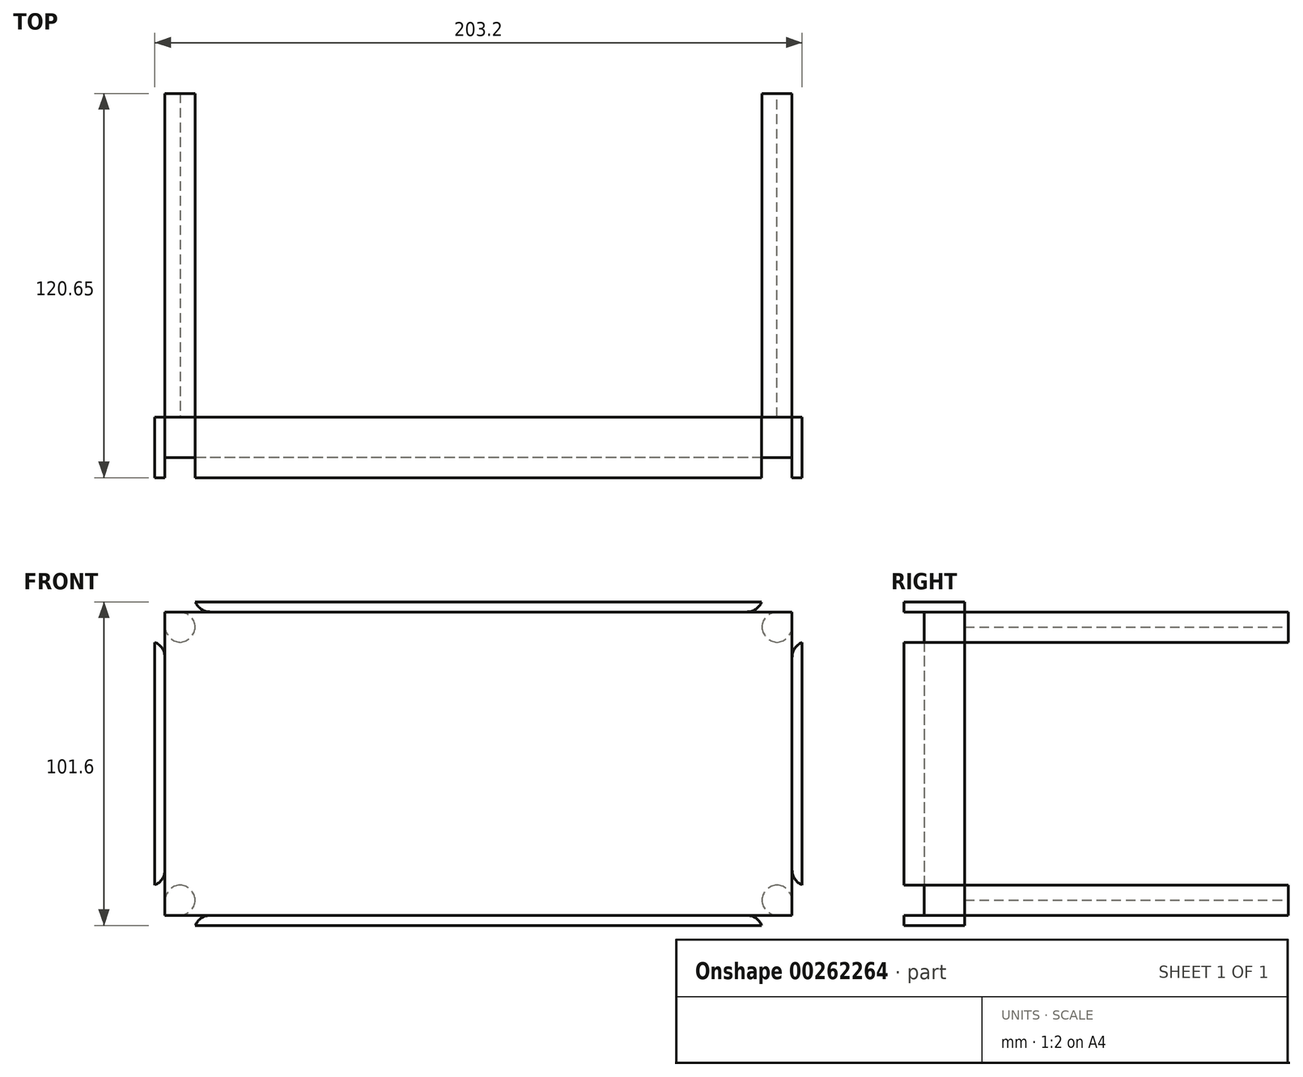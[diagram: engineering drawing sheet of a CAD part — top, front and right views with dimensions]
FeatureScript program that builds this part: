
annotation { "Feature Type Name" : "Feature", "Feature Type Description" : "" }
export const myFeature = defineFeature(function(context is Context, id is Id, definition is map)
    precondition{}
    {
        {
            var Q0;
            Q0=qCreatedBy(makeId("Front.planeOp"),FACE);
            var sketch = newSketch(context, id + "F0", { "sketchPlane" : qUnion([Q0])});
            skLineSegment(sketch, "E0.bottom", {"start": v(101.6, 50.8) * mm, "end": v(-101.6, 50.8) * mm});
            skLineSegment(sketch, "E0.top", {"start": v(101.6, -50.8) * mm, "end": v(-101.6, -50.8) * mm});
            skLineSegment(sketch, "E0.left", {"start": v(101.6, 50.8) * mm, "end": v(101.6, -50.8) * mm});
            skLineSegment(sketch, "E0.right", {"start": v(-101.6, 50.8) * mm, "end": v(-101.6, -50.8) * mm});
            skPoint(sketch, "E0.middle", {"position": v(0, 0) * mm});
            skLineSegment(sketch, "E1.bottom", {"start": v(98.43, 47.62) * mm, "end": v(-98.43, 47.62) * mm});
            skLineSegment(sketch, "E1.top", {"start": v(98.43, -47.63) * mm, "end": v(-98.43, -47.63) * mm});
            skLineSegment(sketch, "E1.left", {"start": v(98.43, 47.62) * mm, "end": v(98.43, -47.63) * mm});
            skLineSegment(sketch, "E1.right", {"start": v(-98.43, 47.63) * mm, "end": v(-98.43, -47.63) * mm});
            skLineSegment(sketch, "E2.bottom", {"start": v(-101.6, 50.8) * mm, "end": v(-88.9, 50.8) * mm});
            skLineSegment(sketch, "E2.top", {"start": v(-101.6, 38.1) * mm, "end": v(-88.9, 38.1) * mm});
            skLineSegment(sketch, "E2.left", {"start": v(-101.6, 50.8) * mm, "end": v(-101.6, 38.1) * mm});
            skLineSegment(sketch, "E2.right", {"start": v(-88.9, 50.8) * mm, "end": v(-88.9, 38.1) * mm});
            skLineSegment(sketch, "E3.bottom", {"start": v(-101.6, -50.8) * mm, "end": v(-88.9, -50.8) * mm});
            skLineSegment(sketch, "E3.top", {"start": v(-101.6, -38.1) * mm, "end": v(-88.9, -38.1) * mm});
            skLineSegment(sketch, "E3.left", {"start": v(-101.6, -50.8) * mm, "end": v(-101.6, -38.1) * mm});
            skLineSegment(sketch, "E3.right", {"start": v(-88.9, -50.8) * mm, "end": v(-88.9, -38.1) * mm});
            skLineSegment(sketch, "E4.bottom", {"start": v(101.6, -50.8) * mm, "end": v(88.9, -50.8) * mm});
            skLineSegment(sketch, "E4.top", {"start": v(101.6, -38.1) * mm, "end": v(88.9, -38.1) * mm});
            skLineSegment(sketch, "E4.left", {"start": v(101.6, -50.8) * mm, "end": v(101.6, -38.1) * mm});
            skLineSegment(sketch, "E4.right", {"start": v(88.9, -50.8) * mm, "end": v(88.9, -38.1) * mm});
            skLineSegment(sketch, "E5.bottom", {"start": v(101.6, 50.8) * mm, "end": v(88.9, 50.8) * mm});
            skLineSegment(sketch, "E5.top", {"start": v(101.6, 38.1) * mm, "end": v(88.9, 38.1) * mm});
            skLineSegment(sketch, "E5.left", {"start": v(101.6, 50.8) * mm, "end": v(101.6, 38.1) * mm});
            skLineSegment(sketch, "E5.right", {"start": v(88.9, 50.8) * mm, "end": v(88.9, 38.1) * mm});
            skSolve(sketch);
        }
        {
            var Q0;
            {var subQ19=sQuery(id+"F0.wireOp",EDGE,"E5.right");var subQ20=sQuery(id+"F0.wireOp",EDGE,"E1.bottom");var subQ21=makeQuery(id+"F0.imprint","INTERSECT",VERTEX,{"derivedFrom":[subQ20,subQ19]});Q0=makeQuery(id+"F0.imprint","IMPRINT",FACE,{"disambiguationData":[TD([[makeQuery(id+"F0.imprint","IMPRINT",EDGE,{"disambiguationData":[TD([[subQ21,-1.0]])],"derivedFrom":subQ20}),1.0]])]});}
            var Q1;
            {var subQ0=sQuery(id+"F0.wireOp",EDGE,"E1.right");var subQ1=sQuery(id+"F0.wireOp",EDGE,"E1.bottom");var subQ2=makeQuery(id+"F0.imprint","INTERSECT",VERTEX,{"derivedFrom":[subQ1,subQ0]});Q1=makeQuery(id+"F0.imprint","IMPRINT",FACE,{"disambiguationData":[TD([[makeQuery(id+"F0.imprint","IMPRINT",EDGE,{"disambiguationData":[TD([[subQ2,1.0]])],"derivedFrom":subQ1}),1.0]])]});}
            var Q2;
            {var subQ0=sQuery(id+"F0.wireOp",EDGE,"E1.right");var subQ1=sQuery(id+"F0.wireOp",EDGE,"E1.top");var subQ2=makeQuery(id+"F0.imprint","INTERSECT",VERTEX,{"derivedFrom":[subQ1,subQ0]});Q2=makeQuery(id+"F0.imprint","IMPRINT",FACE,{"disambiguationData":[TD([[makeQuery(id+"F0.imprint","IMPRINT",EDGE,{"disambiguationData":[TD([[subQ2,1.0]])],"derivedFrom":subQ1}),-1.0]])]});}
            var Q3;
            {var subQ0=sQuery(id+"F0.wireOp",EDGE,"E1.left");var subQ1=sQuery(id+"F0.wireOp",EDGE,"E1.bottom");var subQ2=makeQuery(id+"F0.imprint","INTERSECT",VERTEX,{"derivedFrom":[subQ1,subQ0]});Q3=makeQuery(id+"F0.imprint","IMPRINT",FACE,{"disambiguationData":[TD([[makeQuery(id+"F0.imprint","IMPRINT",EDGE,{"disambiguationData":[TD([[subQ2,-1.0]])],"derivedFrom":subQ1}),1.0]])]});}
            var Q4;
            {var subQ0=sQuery(id+"F0.wireOp",EDGE,"E1.left");var subQ1=sQuery(id+"F0.wireOp",EDGE,"E1.top");var subQ2=makeQuery(id+"F0.imprint","INTERSECT",VERTEX,{"derivedFrom":[subQ1,subQ0]});Q4=makeQuery(id+"F0.imprint","IMPRINT",FACE,{"disambiguationData":[TD([[makeQuery(id+"F0.imprint","IMPRINT",EDGE,{"disambiguationData":[TD([[subQ2,-1.0]])],"derivedFrom":subQ1}),-1.0]])]});}
            extrude(context, id + "F1", {"entities" : qUnion([Q0, Q1, Q2, Q3, Q4]), "depth" : 12.7 * mm});
        }
        {
            var Q0;
            {var subQ0=sQuery(id+"F0.wireOp",EDGE,"E0.right");Q0=makeQuery(id+"F0.imprint","IMPRINT",FACE,{"disambiguationData":[TD([[makeQuery(id+"F0.imprint","IMPRINT",EDGE,{"derivedFrom":subQ0}),1.0]])]});}
            var Q1;
            {var subQ8=sQuery(id+"F0.wireOp",EDGE,"E2.bottom");Q1=makeQuery(id+"F0.imprint","IMPRINT",FACE,{"disambiguationData":[TD([[makeQuery(id+"F0.imprint","IMPRINT",EDGE,{"derivedFrom":subQ8}),-1.0]])]});}
            var Q2;
            {var subQ0=sQuery(id+"F0.wireOp",EDGE,"E0.bottom");Q2=makeQuery(id+"F0.imprint","IMPRINT",FACE,{"disambiguationData":[TD([[makeQuery(id+"F0.imprint","IMPRINT",EDGE,{"derivedFrom":subQ0}),1.0]])]});}
            var Q3;
            {var subQ8=sQuery(id+"F0.wireOp",EDGE,"E5.bottom");Q3=makeQuery(id+"F0.imprint","IMPRINT",FACE,{"disambiguationData":[TD([[makeQuery(id+"F0.imprint","IMPRINT",EDGE,{"derivedFrom":subQ8}),1.0]])]});}
            var Q4;
            {var subQ0=sQuery(id+"F0.wireOp",EDGE,"E0.left");Q4=makeQuery(id+"F0.imprint","IMPRINT",FACE,{"disambiguationData":[TD([[makeQuery(id+"F0.imprint","IMPRINT",EDGE,{"derivedFrom":subQ0}),-1.0]])]});}
            var Q5;
            {var subQ0=sQuery(id+"F0.wireOp",EDGE,"E0.top");Q5=makeQuery(id+"F0.imprint","IMPRINT",FACE,{"disambiguationData":[TD([[makeQuery(id+"F0.imprint","IMPRINT",EDGE,{"derivedFrom":subQ0}),-1.0]])]});}
            var Q6;
            {var subQ4=sQuery(id+"F0.wireOp",EDGE,"E4.bottom");Q6=makeQuery(id+"F0.imprint","IMPRINT",FACE,{"disambiguationData":[TD([[makeQuery(id+"F0.imprint","IMPRINT",EDGE,{"derivedFrom":subQ4}),-1.0]])]});}
            var Q7;
            {var subQ4=sQuery(id+"F0.wireOp",EDGE,"E3.bottom");Q7=makeQuery(id+"F0.imprint","IMPRINT",FACE,{"disambiguationData":[TD([[makeQuery(id+"F0.imprint","IMPRINT",EDGE,{"derivedFrom":subQ4}),1.0]])]});}
            extrude(context, id + "F2", {"entities" : qUnion([Q0, Q1, Q2, Q3, Q4, Q5, Q6, Q7]), "depth" : 19.05 * mm});
        }
        {
            var Q0;
            {var subQ0=sQuery(id+"F0.wireOp",EDGE,"E1.right");var subQ1=sQuery(id+"F0.wireOp",EDGE,"E1.bottom");var subQ2=makeQuery(id+"F0.imprint","INTERSECT",VERTEX,{"derivedFrom":[subQ1,subQ0]});Q0=makeQuery(id+"F0.imprint","IMPRINT",FACE,{"disambiguationData":[TD([[makeQuery(id+"F0.imprint","IMPRINT",EDGE,{"disambiguationData":[TD([[subQ2,1.0]])],"derivedFrom":subQ1}),1.0]])]});}
            var Q1;
            {var subQ8=sQuery(id+"F0.wireOp",EDGE,"E2.bottom");Q1=makeQuery(id+"F0.imprint","IMPRINT",FACE,{"disambiguationData":[TD([[makeQuery(id+"F0.imprint","IMPRINT",EDGE,{"derivedFrom":subQ8}),-1.0]])]});}
            var Q2;
            {var subQ0=sQuery(id+"F0.wireOp",EDGE,"E1.right");var subQ1=sQuery(id+"F0.wireOp",EDGE,"E1.top");var subQ2=makeQuery(id+"F0.imprint","INTERSECT",VERTEX,{"derivedFrom":[subQ1,subQ0]});Q2=makeQuery(id+"F0.imprint","IMPRINT",FACE,{"disambiguationData":[TD([[makeQuery(id+"F0.imprint","IMPRINT",EDGE,{"disambiguationData":[TD([[subQ2,1.0]])],"derivedFrom":subQ1}),-1.0]])]});}
            var Q3;
            {var subQ4=sQuery(id+"F0.wireOp",EDGE,"E3.bottom");Q3=makeQuery(id+"F0.imprint","IMPRINT",FACE,{"disambiguationData":[TD([[makeQuery(id+"F0.imprint","IMPRINT",EDGE,{"derivedFrom":subQ4}),1.0]])]});}
            var Q4;
            {var subQ0=sQuery(id+"F0.wireOp",EDGE,"E1.left");var subQ1=sQuery(id+"F0.wireOp",EDGE,"E1.top");var subQ2=makeQuery(id+"F0.imprint","INTERSECT",VERTEX,{"derivedFrom":[subQ1,subQ0]});Q4=makeQuery(id+"F0.imprint","IMPRINT",FACE,{"disambiguationData":[TD([[makeQuery(id+"F0.imprint","IMPRINT",EDGE,{"disambiguationData":[TD([[subQ2,-1.0]])],"derivedFrom":subQ1}),-1.0]])]});}
            var Q5;
            {var subQ4=sQuery(id+"F0.wireOp",EDGE,"E4.bottom");Q5=makeQuery(id+"F0.imprint","IMPRINT",FACE,{"disambiguationData":[TD([[makeQuery(id+"F0.imprint","IMPRINT",EDGE,{"derivedFrom":subQ4}),-1.0]])]});}
            var Q6;
            {var subQ0=sQuery(id+"F0.wireOp",EDGE,"E1.left");var subQ1=sQuery(id+"F0.wireOp",EDGE,"E1.bottom");var subQ2=makeQuery(id+"F0.imprint","INTERSECT",VERTEX,{"derivedFrom":[subQ1,subQ0]});Q6=makeQuery(id+"F0.imprint","IMPRINT",FACE,{"disambiguationData":[TD([[makeQuery(id+"F0.imprint","IMPRINT",EDGE,{"disambiguationData":[TD([[subQ2,-1.0]])],"derivedFrom":subQ1}),1.0]])]});}
            var Q7;
            {var subQ8=sQuery(id+"F0.wireOp",EDGE,"E5.bottom");Q7=makeQuery(id+"F0.imprint","IMPRINT",FACE,{"disambiguationData":[TD([[makeQuery(id+"F0.imprint","IMPRINT",EDGE,{"derivedFrom":subQ8}),1.0]])]});}
            extrude(context, id + "F3", {"entities" : qUnion([Q0, Q1, Q2, Q3, Q4, Q5, Q6, Q7]), "oppositeDirection" : true, "depth" : 101.6 * mm});
        }
        {
            var Q0;
            Q0=makeQuery(id+"F2.opExtrude","SWEPT_EDGE",EDGE,{"disambiguationData":[OSD([sQuery(id+"F0.wireOp",EDGE,"E1.top"),sQuery(id+"F0.wireOp",EDGE,"E1.left")])]});
            var Q1;
            Q1=makeQuery(id+"F2.opExtrude","SWEPT_EDGE",EDGE,{"disambiguationData":[OSD([sQuery(id+"F0.wireOp",EDGE,"E1.bottom"),sQuery(id+"F0.wireOp",EDGE,"E1.left")])]});
            var Q2;
            Q2=makeQuery(id+"F2.opExtrude","SWEPT_EDGE",EDGE,{"disambiguationData":[OSD([sQuery(id+"F0.wireOp",EDGE,"E1.top"),sQuery(id+"F0.wireOp",EDGE,"E1.right")])]});
            var Q3;
            Q3=makeQuery(id+"F2.opExtrude","SWEPT_EDGE",EDGE,{"disambiguationData":[OSD([sQuery(id+"F0.wireOp",EDGE,"E1.bottom"),sQuery(id+"F0.wireOp",EDGE,"E1.right")])]});
            var Q4;
            Q4=makeQuery(id+"F2.opExtrude","SWEPT_EDGE",EDGE,{"disambiguationData":[OSD([sQuery(id+"F0.wireOp",EDGE,"E4.bottom"),sQuery(id+"F0.wireOp",EDGE,"E4.left")])]});
            var Q5;
            Q5=makeQuery(id+"F2.opExtrude","SWEPT_EDGE",EDGE,{"disambiguationData":[OSD([sQuery(id+"F0.wireOp",EDGE,"E5.bottom"),sQuery(id+"F0.wireOp",EDGE,"E5.left")])]});
            var Q6;
            Q6=makeQuery(id+"F2.opExtrude","SWEPT_EDGE",EDGE,{"disambiguationData":[OSD([sQuery(id+"F0.wireOp",EDGE,"E2.bottom"),sQuery(id+"F0.wireOp",EDGE,"E2.left")])]});
            var Q7;
            Q7=makeQuery(id+"F2.opExtrude","SWEPT_EDGE",EDGE,{"disambiguationData":[OSD([sQuery(id+"F0.wireOp",EDGE,"E3.bottom"),sQuery(id+"F0.wireOp",EDGE,"E3.left")])]});
            var Q8;
            Q8=makeQuery(id+"F3.opExtrude","SWEPT_EDGE",EDGE,{"disambiguationData":[OSD([sQuery(id+"F0.wireOp",EDGE,"E5.bottom"),sQuery(id+"F0.wireOp",EDGE,"E5.left")])]});
            var Q9;
            Q9=makeQuery(id+"F3.opExtrude","SWEPT_EDGE",EDGE,{"disambiguationData":[OSD([sQuery(id+"F0.wireOp",EDGE,"E5.top"),sQuery(id+"F0.wireOp",EDGE,"E5.right")])]});
            var Q10;
            Q10=makeQuery(id+"F3.opExtrude","SWEPT_EDGE",EDGE,{"disambiguationData":[OSD([sQuery(id+"F0.wireOp",EDGE,"E0.bottom"),sQuery(id+"F0.wireOp",EDGE,"E5.bottom"),sQuery(id+"F0.wireOp",EDGE,"E5.right")])]});
            var Q11;
            Q11=makeQuery(id+"F3.opExtrude","SWEPT_EDGE",EDGE,{"disambiguationData":[OSD([sQuery(id+"F0.wireOp",EDGE,"E0.left"),sQuery(id+"F0.wireOp",EDGE,"E5.top"),sQuery(id+"F0.wireOp",EDGE,"E5.left")])]});
            var Q12;
            Q12=makeQuery(id+"F3.opExtrude","SWEPT_EDGE",EDGE,{"disambiguationData":[OSD([sQuery(id+"F0.wireOp",EDGE,"E0.left"),sQuery(id+"F0.wireOp",EDGE,"E4.top"),sQuery(id+"F0.wireOp",EDGE,"E4.left")])]});
            var Q13;
            Q13=makeQuery(id+"F3.opExtrude","SWEPT_EDGE",EDGE,{"disambiguationData":[OSD([sQuery(id+"F0.wireOp",EDGE,"E4.bottom"),sQuery(id+"F0.wireOp",EDGE,"E4.left")])]});
            var Q14;
            Q14=makeQuery(id+"F3.opExtrude","SWEPT_EDGE",EDGE,{"disambiguationData":[OSD([sQuery(id+"F0.wireOp",EDGE,"E4.top"),sQuery(id+"F0.wireOp",EDGE,"E4.right")])]});
            var Q15;
            Q15=makeQuery(id+"F3.opExtrude","SWEPT_EDGE",EDGE,{"disambiguationData":[OSD([sQuery(id+"F0.wireOp",EDGE,"E0.top"),sQuery(id+"F0.wireOp",EDGE,"E4.bottom"),sQuery(id+"F0.wireOp",EDGE,"E4.right")])]});
            var Q16;
            Q16=makeQuery(id+"F3.opExtrude","SWEPT_EDGE",EDGE,{"disambiguationData":[OSD([sQuery(id+"F0.wireOp",EDGE,"E3.bottom"),sQuery(id+"F0.wireOp",EDGE,"E3.left")])]});
            var Q17;
            Q17=makeQuery(id+"F3.opExtrude","SWEPT_EDGE",EDGE,{"disambiguationData":[OSD([sQuery(id+"F0.wireOp",EDGE,"E0.top"),sQuery(id+"F0.wireOp",EDGE,"E3.bottom"),sQuery(id+"F0.wireOp",EDGE,"E3.right")])]});
            var Q18;
            Q18=makeQuery(id+"F3.opExtrude","SWEPT_EDGE",EDGE,{"disambiguationData":[OSD([sQuery(id+"F0.wireOp",EDGE,"E0.right"),sQuery(id+"F0.wireOp",EDGE,"E3.top"),sQuery(id+"F0.wireOp",EDGE,"E3.left")])]});
            var Q19;
            Q19=makeQuery(id+"F3.opExtrude","SWEPT_EDGE",EDGE,{"disambiguationData":[OSD([sQuery(id+"F0.wireOp",EDGE,"E3.top"),sQuery(id+"F0.wireOp",EDGE,"E3.right")])]});
            var Q20;
            Q20=makeQuery(id+"F3.opExtrude","SWEPT_EDGE",EDGE,{"disambiguationData":[OSD([sQuery(id+"F0.wireOp",EDGE,"E0.right"),sQuery(id+"F0.wireOp",EDGE,"E2.top"),sQuery(id+"F0.wireOp",EDGE,"E2.left")])]});
            var Q21;
            Q21=makeQuery(id+"F3.opExtrude","SWEPT_EDGE",EDGE,{"disambiguationData":[OSD([sQuery(id+"F0.wireOp",EDGE,"E2.bottom"),sQuery(id+"F0.wireOp",EDGE,"E2.left")])]});
            var Q22;
            Q22=makeQuery(id+"F3.opExtrude","SWEPT_EDGE",EDGE,{"disambiguationData":[OSD([sQuery(id+"F0.wireOp",EDGE,"E0.bottom"),sQuery(id+"F0.wireOp",EDGE,"E2.bottom"),sQuery(id+"F0.wireOp",EDGE,"E2.right")])]});
            var Q23;
            Q23=makeQuery(id+"F3.opExtrude","SWEPT_EDGE",EDGE,{"disambiguationData":[OSD([sQuery(id+"F0.wireOp",EDGE,"E2.top"),sQuery(id+"F0.wireOp",EDGE,"E2.right")])]});
            fillet(context, id + "F4", {"entities" : qUnion([Q0, Q1, Q2, Q3, Q4, Q5, Q6, Q7, Q8, Q9, Q10, Q11, Q12, Q13, Q14, Q15, Q16, Q17, Q18, Q19, Q20, Q21, Q22, Q23]), "radius" : 5.08 * mm, "tangentPropagation" : true, "allowEdgeOverflow" : false});
        }
    });
